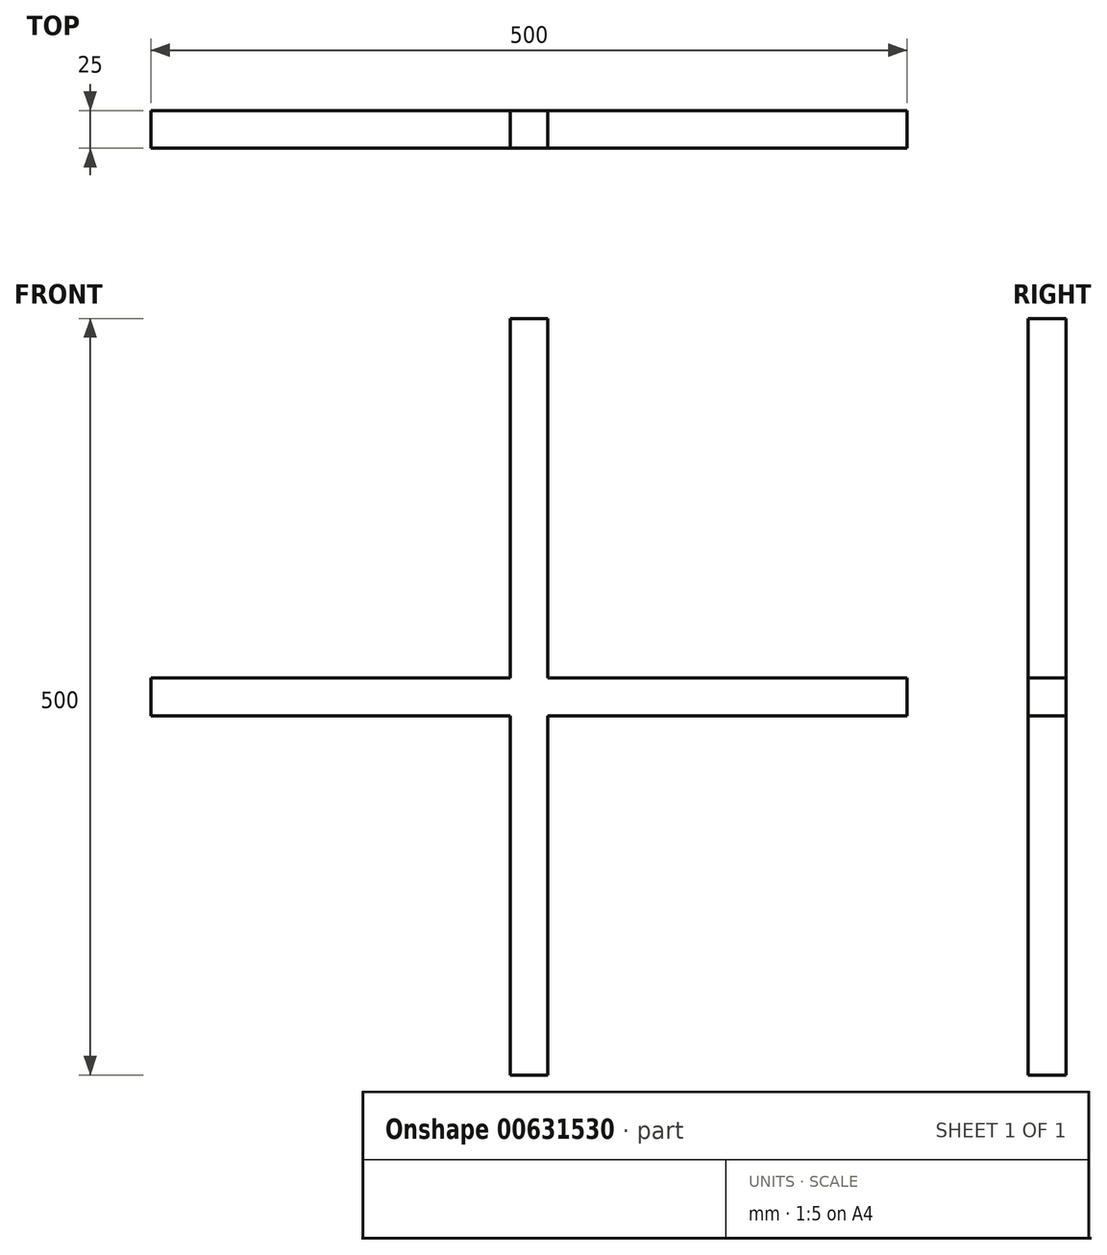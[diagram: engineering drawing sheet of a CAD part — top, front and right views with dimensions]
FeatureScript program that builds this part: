
annotation { "Feature Type Name" : "Feature", "Feature Type Description" : "" }
export const myFeature = defineFeature(function(context is Context, id is Id, definition is map)
    precondition{}
    {
        {
            var Q0;
            Q0=qCreatedBy(makeId("Front.planeOp"),FACE);
            var sketch = newSketch(context, id + "F0", { "sketchPlane" : qUnion([Q0])});
            skLineSegment(sketch, "E0.bottom", {"start": v(0, 0) * mm, "end": v(25, 0) * mm});
            skLineSegment(sketch, "E0.top", {"start": v(0, 250) * mm, "end": v(25, 250) * mm});
            skLineSegment(sketch, "E0.left", {"start": v(0, 0) * mm, "end": v(0, 250) * mm});
            skLineSegment(sketch, "E0.right", {"start": v(25, 0) * mm, "end": v(25, 250) * mm});
            skSolve(sketch);
        }
        {
            var Q0;
            Q0=makeQuery(id+"F0.imprint","IMPRINT",FACE,{"disambiguationData":[TD([[makeQuery(id+"F0.imprint","IMPRINT",EDGE,{"derivedFrom":sQuery(id+"F0.wireOp",EDGE,"E0.bottom")}),1.0]])]});
            extrude(context, id + "F1", {"entities" : qUnion([Q0]), "depth" : 25 * mm, "offsetDistance" : 25 * mm});
        }
        {
            var Q0;
            Q0=makeQuery(id+"F1.opExtrude","SWEPT_FACE",FACE,{"disambiguationData":[OSD([sQuery(id+"F0.wireOp",EDGE,"E0.bottom")])]});
            var sketch = newSketch(context, id + "F2", { "sketchPlane" : qUnion([Q0])});
            skLineSegment(sketch, "E1", {"start": v(12.5, 0) * mm, "end": v(12.5, 25) * mm});
            skSolve(sketch);
        }
        {
            var Q0;
            Q0=makeQuery(id+"F1.opExtrude","SWEPT_BODY",BODY,{"disambiguationData":[OSD([sQuery(id+"F0.wireOp",EDGE,"E0.bottom"),sQuery(id+"F0.wireOp",EDGE,"E0.top"),sQuery(id+"F0.wireOp",EDGE,"E0.left"),sQuery(id+"F0.wireOp",EDGE,"E0.right")])]});
            var Q1;
            Q1=sQuery(id+"F2.wireOp",EDGE,"E1");
            circularPattern(context, id + "F3", {"entities" : qUnion([Q0]), "axis" : qUnion([Q1]), "angle" : 360 * degree, "instanceCount" : 4, "equalSpace" : true});
        }
        {
            var Q0;
            Q0=makeQuery(id+"F3.opPattern","COPY",BODY,{"derivedFrom":makeQuery(id+"F1.opExtrude","SWEPT_BODY",BODY,{"disambiguationData":[OSD([sQuery(id+"F0.wireOp",EDGE,"E0.bottom"),sQuery(id+"F0.wireOp",EDGE,"E0.top"),sQuery(id+"F0.wireOp",EDGE,"E0.left"),sQuery(id+"F0.wireOp",EDGE,"E0.right")])]}),"instanceName":"2"});
            var Q1;
            Q1=makeQuery(id+"F3.opPattern","COPY",BODY,{"derivedFrom":makeQuery(id+"F1.opExtrude","SWEPT_BODY",BODY,{"disambiguationData":[OSD([sQuery(id+"F0.wireOp",EDGE,"E0.bottom"),sQuery(id+"F0.wireOp",EDGE,"E0.top"),sQuery(id+"F0.wireOp",EDGE,"E0.left"),sQuery(id+"F0.wireOp",EDGE,"E0.right")])]}),"instanceName":"1"});
            var Q2;
            Q2=makeQuery(id+"F1.opExtrude","SWEPT_BODY",BODY,{"disambiguationData":[OSD([sQuery(id+"F0.wireOp",EDGE,"E0.bottom"),sQuery(id+"F0.wireOp",EDGE,"E0.top"),sQuery(id+"F0.wireOp",EDGE,"E0.left"),sQuery(id+"F0.wireOp",EDGE,"E0.right")])]});
            var Q3;
            Q3=makeQuery(id+"F3.opPattern","COPY",BODY,{"derivedFrom":makeQuery(id+"F1.opExtrude","SWEPT_BODY",BODY,{"disambiguationData":[OSD([sQuery(id+"F0.wireOp",EDGE,"E0.bottom"),sQuery(id+"F0.wireOp",EDGE,"E0.top"),sQuery(id+"F0.wireOp",EDGE,"E0.left"),sQuery(id+"F0.wireOp",EDGE,"E0.right")])]}),"instanceName":"3"});
            booleanBodies(context, id + "F4", {"operationType" : BooleanOperationType.UNION, "tools" : qUnion([Q0, Q1, Q2, Q3])});
        }
    });
